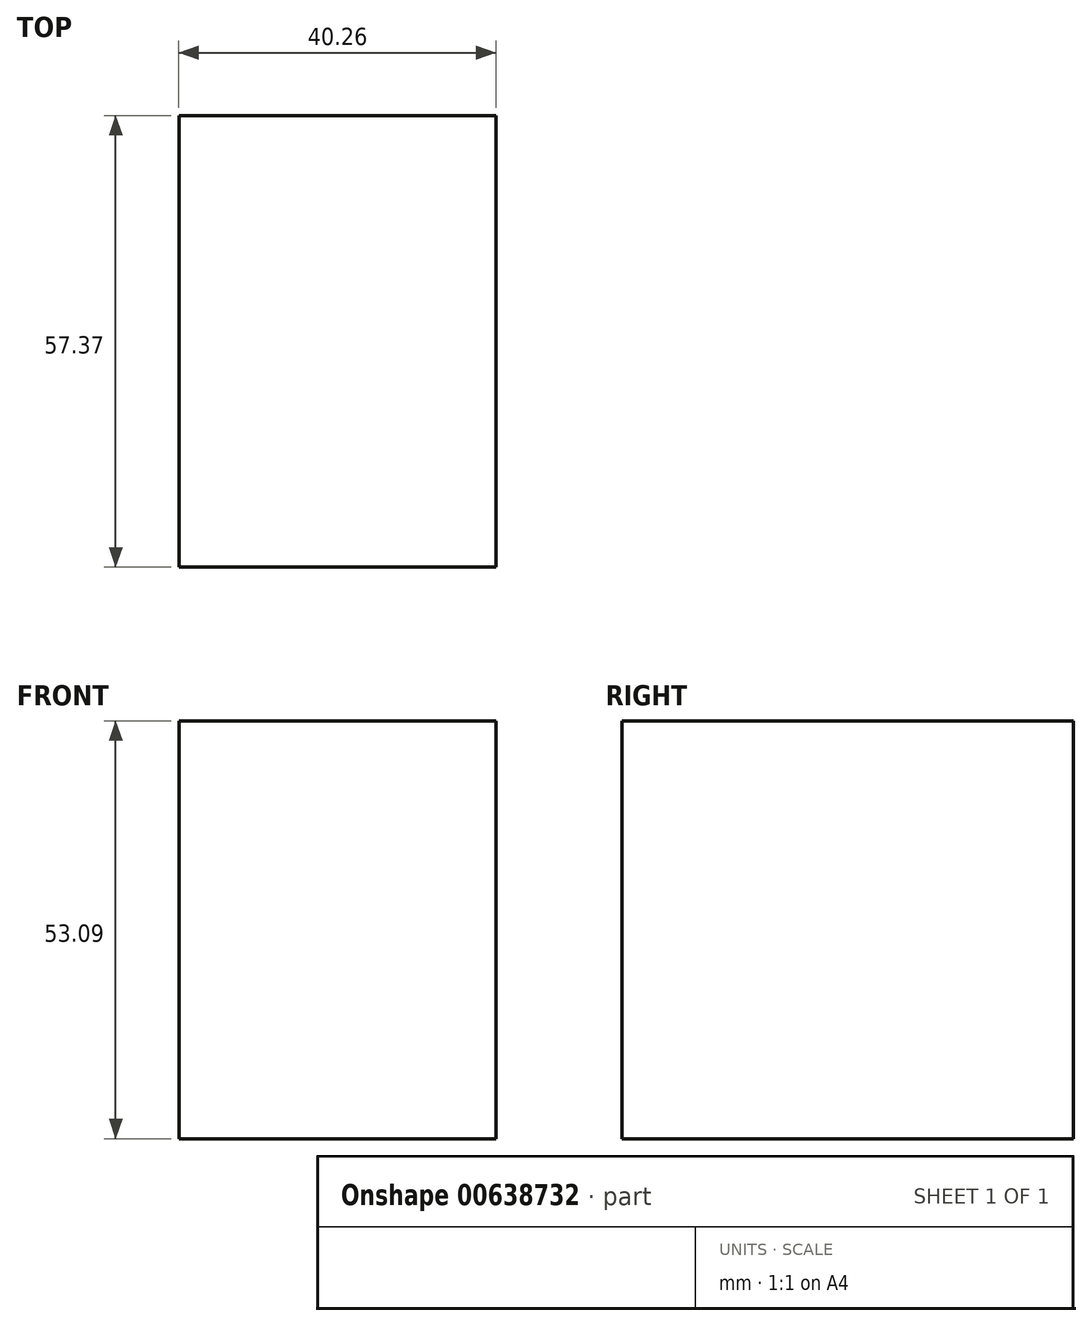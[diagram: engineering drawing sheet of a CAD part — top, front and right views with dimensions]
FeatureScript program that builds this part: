
annotation { "Feature Type Name" : "Feature", "Feature Type Description" : "" }
export const myFeature = defineFeature(function(context is Context, id is Id, definition is map)
    precondition{}
    {
        {
            var Q0;
            Q0=qCreatedBy(makeId("Top.planeOp"),FACE);
            var sketch = newSketch(context, id + "F0", { "sketchPlane" : qUnion([Q0])});
            skLineSegment(sketch, "E0.bottom", {"start": v(0, 0) * mm, "end": v(-40.26, 0) * mm});
            skLineSegment(sketch, "E0.top", {"start": v(0, 57.37) * mm, "end": v(-40.26, 57.37) * mm});
            skLineSegment(sketch, "E0.left", {"start": v(0, 0) * mm, "end": v(0, 57.37) * mm});
            skLineSegment(sketch, "E0.right", {"start": v(-40.26, 0) * mm, "end": v(-40.26, 57.37) * mm});
            skSolve(sketch);
        }
        {
            var Q0;
            Q0=makeQuery(id+"F0.imprint","IMPRINT",FACE,{"disambiguationData":[TD([[makeQuery(id+"F0.imprint","IMPRINT",EDGE,{"derivedFrom":sQuery(id+"F0.wireOp",EDGE,"E0.bottom")}),-1.0]])]});
            extrude(context, id + "F1", {"entities" : qUnion([Q0]), "depth" : 53.1 * mm, "offsetDistance" : 25.4 * mm});
        }
    });
